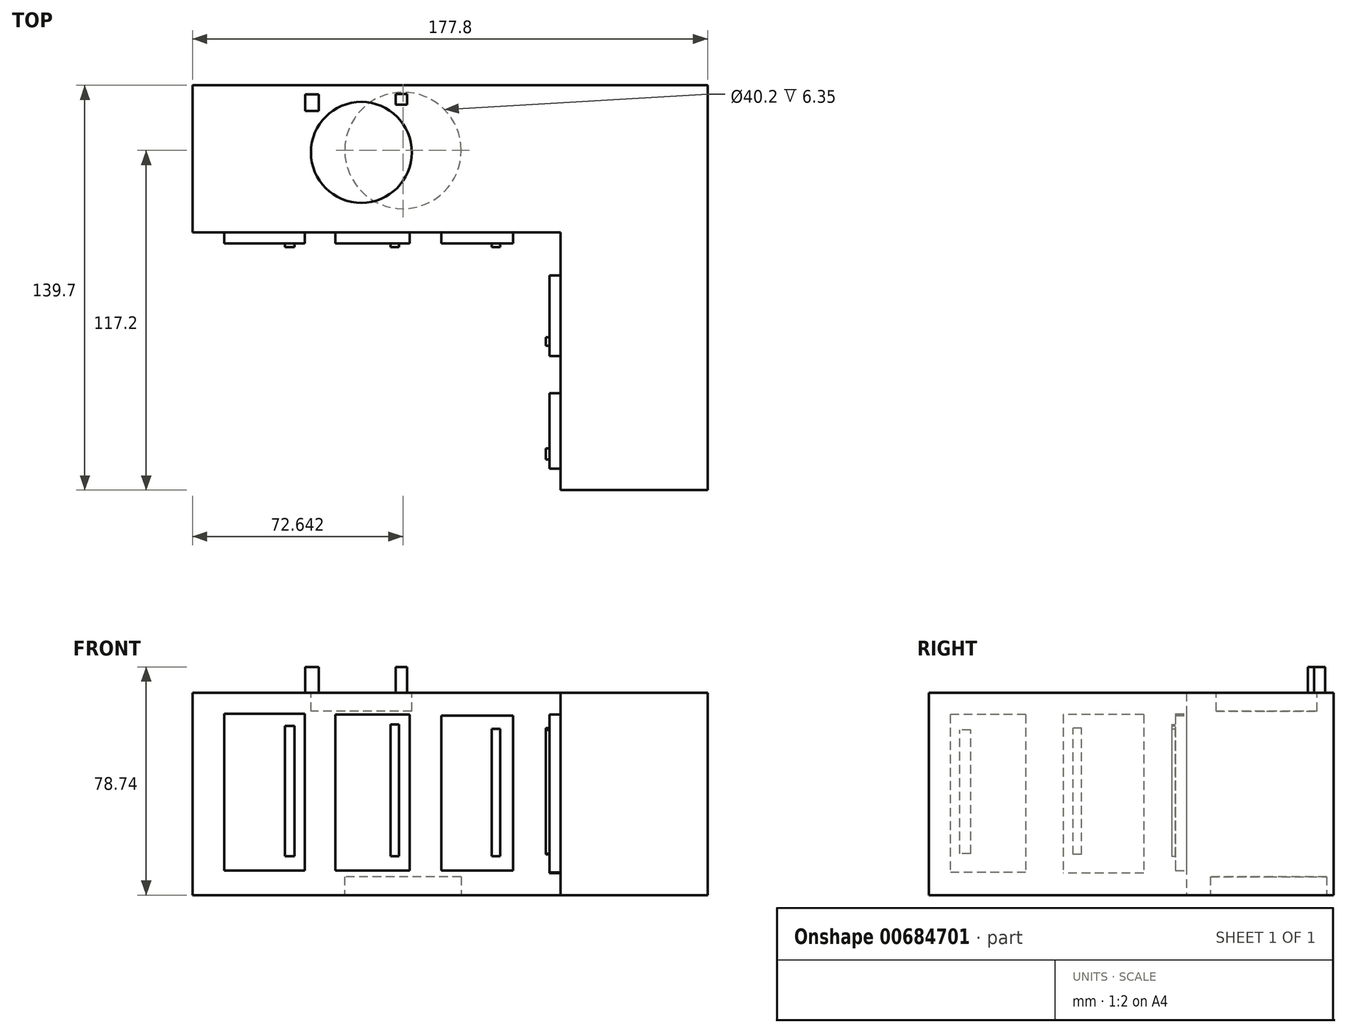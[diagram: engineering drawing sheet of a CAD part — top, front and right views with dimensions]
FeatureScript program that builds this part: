
annotation { "Feature Type Name" : "Feature", "Feature Type Description" : "" }
export const myFeature = defineFeature(function(context is Context, id is Id, definition is map)
    precondition{}
    {
        {
            var Q0;
            Q0=qCreatedBy(makeId("Top.planeOp"),FACE);
            var sketch = newSketch(context, id + "F0", { "sketchPlane" : qUnion([Q0])});
            skLineSegment(sketch, "E0.bottom", {"start": v(-90.51, 80.44) * mm, "end": v(87.29, 80.44) * mm});
            skLineSegment(sketch, "E0.top", {"start": v(-90.51, 29.64) * mm, "end": v(87.29, 29.64) * mm});
            skLineSegment(sketch, "E0.left", {"start": v(-90.51, 80.44) * mm, "end": v(-90.51, 29.64) * mm});
            skLineSegment(sketch, "E0.right", {"start": v(87.29, 80.44) * mm, "end": v(87.29, 29.64) * mm});
            skLineSegment(sketch, "E1.bottom", {"start": v(87.29, 29.64) * mm, "end": v(36.49, 29.64) * mm});
            skLineSegment(sketch, "E1.top", {"start": v(87.29, -59.26) * mm, "end": v(36.49, -59.26) * mm});
            skLineSegment(sketch, "E1.left", {"start": v(87.29, 29.64) * mm, "end": v(87.29, -59.26) * mm});
            skLineSegment(sketch, "E1.right", {"start": v(36.49, 29.64) * mm, "end": v(36.49, -59.26) * mm});
            skSolve(sketch);
        }
        {
            var Q0;
            Q0=qSketchRegion(id+"F0",true);
            extrude(context, id + "F1", {"entities" : qUnion([Q0]), "depth" : 69.85 * mm, "offsetDistance" : 25.4 * mm});
        }
        {
            var Q0;
            Q0=qCreatedBy(makeId("Top.planeOp"),FACE);
            var sketch = newSketch(context, id + "F2", { "sketchPlane" : qUnion([Q0])});
            skCircle(sketch, "E2", {"center": v(-17.87, 57.94) * mm, "radius": 20.1 * mm});
            skSolve(sketch);
        }
        {
            var Q0;
            Q0=qSketchRegion(id+"F2",true);
            extrude(context, id + "F3", {"entities" : qUnion([Q0]), "operationType" : NewBodyOperationType.REMOVE, "oppositeDirection" : true, "depth" : -6.35 * mm, "offsetDistance" : 25.4 * mm});
        }
        {
            var Q0;
            Q0=makeQuery(id+"F1.opExtrude","CAP_FACE",FACE,{"disambiguationData":[OSD([sQuery(id+"F0.wireOp",EDGE,"E0.bottom"),sQuery(id+"F0.wireOp",EDGE,"E0.top"),sQuery(id+"F0.wireOp",EDGE,"E0.left"),sQuery(id+"F0.wireOp",EDGE,"E0.right"),sQuery(id+"F0.wireOp",EDGE,"E1.top"),sQuery(id+"F0.wireOp",EDGE,"E1.left"),sQuery(id+"F0.wireOp",EDGE,"E1.right")])],"isStart":false});
            var sketch = newSketch(context, id + "F4", { "sketchPlane" : qUnion([Q0])});
            skCircle(sketch, "E3", {"center": v(-32.23, 57.3) * mm, "radius": 17.41 * mm});
            skSolve(sketch);
        }
        {
            var Q0;
            Q0=qSketchRegion(id+"F4",true);
            extrude(context, id + "F5", {"entities" : qUnion([Q0]), "operationType" : NewBodyOperationType.REMOVE, "oppositeDirection" : true, "depth" : 6.35 * mm, "offsetDistance" : 25.4 * mm});
        }
        {
            var Q0;
            Q0=makeQuery(id+"F1.opExtrude","CAP_FACE",FACE,{"disambiguationData":[OSD([sQuery(id+"F0.wireOp",EDGE,"E0.bottom"),sQuery(id+"F0.wireOp",EDGE,"E0.top"),sQuery(id+"F0.wireOp",EDGE,"E0.left"),sQuery(id+"F0.wireOp",EDGE,"E0.right"),sQuery(id+"F0.wireOp",EDGE,"E1.top"),sQuery(id+"F0.wireOp",EDGE,"E1.left"),sQuery(id+"F0.wireOp",EDGE,"E1.right")])],"isStart":false});
            var sketch = newSketch(context, id + "F6", { "sketchPlane" : qUnion([Q0])});
            skLineSegment(sketch, "E4.bottom", {"start": v(-51.56, 77.25) * mm, "end": v(-46.96, 77.25) * mm});
            skLineSegment(sketch, "E4.top", {"start": v(-51.56, 71.58) * mm, "end": v(-46.96, 71.58) * mm});
            skLineSegment(sketch, "E4.left", {"start": v(-51.56, 77.25) * mm, "end": v(-51.56, 71.58) * mm});
            skLineSegment(sketch, "E4.right", {"start": v(-46.96, 77.25) * mm, "end": v(-46.96, 71.58) * mm});
            skLineSegment(sketch, "E5.bottom", {"start": v(-20.42, 77.46) * mm, "end": v(-16.41, 77.46) * mm});
            skLineSegment(sketch, "E5.top", {"start": v(-20.42, 73.7) * mm, "end": v(-16.41, 73.7) * mm});
            skLineSegment(sketch, "E5.left", {"start": v(-20.42, 77.46) * mm, "end": v(-20.42, 73.7) * mm});
            skLineSegment(sketch, "E5.right", {"start": v(-16.41, 77.46) * mm, "end": v(-16.41, 73.7) * mm});
            skSolve(sketch);
        }
        {
            var Q0;
            Q0=qSketchRegion(id+"F6",true);
            extrude(context, id + "F7", {"entities" : qUnion([Q0]), "operationType" : NewBodyOperationType.ADD, "depth" : 8.9 * mm, "offsetDistance" : 25.4 * mm});
        }
        {
            var Q0;
            Q0=makeQuery(id+"F1.opExtrude","SWEPT_FACE",FACE,{"disambiguationData":[OSD([sQuery(id+"F0.wireOp",EDGE,"E0.top")])]});
            var sketch = newSketch(context, id + "F8", { "sketchPlane" : qUnion([Q0])});
            skLineSegment(sketch, "E6.bottom", {"start": v(-79.6, 62.57) * mm, "end": v(-51.8, 62.57) * mm});
            skLineSegment(sketch, "E6.top", {"start": v(-79.6, 8.44) * mm, "end": v(-51.8, 8.44) * mm});
            skLineSegment(sketch, "E6.left", {"start": v(-79.6, 62.57) * mm, "end": v(-79.6, 8.44) * mm});
            skLineSegment(sketch, "E6.right", {"start": v(-51.8, 62.57) * mm, "end": v(-51.8, 8.44) * mm});
            skLineSegment(sketch, "E7.bottom", {"start": v(-41.26, 62.28) * mm, "end": v(-15.51, 62.28) * mm});
            skLineSegment(sketch, "E7.top", {"start": v(-41.26, 8.44) * mm, "end": v(-15.51, 8.44) * mm});
            skLineSegment(sketch, "E7.left", {"start": v(-41.26, 62.28) * mm, "end": v(-41.26, 8.44) * mm});
            skLineSegment(sketch, "E7.right", {"start": v(-15.51, 62.28) * mm, "end": v(-15.51, 8.44) * mm});
            skLineSegment(sketch, "E8.bottom", {"start": v(-4.69, 61.99) * mm, "end": v(20.18, 61.99) * mm});
            skLineSegment(sketch, "E8.top", {"start": v(-4.69, 8.44) * mm, "end": v(20.18, 8.44) * mm});
            skLineSegment(sketch, "E8.left", {"start": v(-4.69, 61.99) * mm, "end": v(-4.69, 8.44) * mm});
            skLineSegment(sketch, "E8.right", {"start": v(20.18, 61.99) * mm, "end": v(20.18, 8.44) * mm});
            skSolve(sketch);
        }
        {
            var Q0;
            Q0=qSketchRegion(id+"F8",true);
            extrude(context, id + "F9", {"entities" : qUnion([Q0]), "operationType" : NewBodyOperationType.ADD, "depth" : 3.8 * mm, "offsetDistance" : 25.4 * mm});
        }
        {
            var Q0;
            Q0=makeQuery(id+"F1.opExtrude","SWEPT_FACE",FACE,{"disambiguationData":[OSD([sQuery(id+"F0.wireOp",EDGE,"E1.right")])]});
            var sketch = newSketch(context, id + "F10", { "sketchPlane" : qUnion([Q0])});
            skLineSegment(sketch, "E9.bottom", {"start": v(-14.85, 62.28) * mm, "end": v(12.95, 62.28) * mm});
            skLineSegment(sketch, "E9.top", {"start": v(-14.85, 7.56) * mm, "end": v(12.95, 7.56) * mm});
            skLineSegment(sketch, "E9.left", {"start": v(-14.85, 62.28) * mm, "end": v(-14.85, 7.56) * mm});
            skLineSegment(sketch, "E9.right", {"start": v(12.95, 62.28) * mm, "end": v(12.95, 7.56) * mm});
            skLineSegment(sketch, "E10.bottom", {"start": v(25.82, 62.28) * mm, "end": v(51.86, 62.28) * mm});
            skLineSegment(sketch, "E10.top", {"start": v(25.82, 7.85) * mm, "end": v(51.86, 7.85) * mm});
            skLineSegment(sketch, "E10.left", {"start": v(25.82, 62.28) * mm, "end": v(25.82, 7.85) * mm});
            skLineSegment(sketch, "E10.right", {"start": v(51.86, 62.28) * mm, "end": v(51.86, 7.85) * mm});
            skSolve(sketch);
        }
        {
            var Q0;
            Q0=qSketchRegion(id+"F10",true);
            extrude(context, id + "F11", {"entities" : qUnion([Q0]), "operationType" : NewBodyOperationType.ADD, "depth" : 3.8 * mm, "offsetDistance" : 25.4 * mm});
        }
        {
            var Q0;
            Q0=makeQuery(id+"F1.opExtrude","SWEPT_FACE",FACE,{"disambiguationData":[OSD([sQuery(id+"F0.wireOp",EDGE,"E0.top")])]});
            var sketch = newSketch(context, id + "F12", { "sketchPlane" : qUnion([Q0])});
            skLineSegment(sketch, "E11.bottom", {"start": v(-58.65, 58.4) * mm, "end": v(-55.35, 58.4) * mm});
            skLineSegment(sketch, "E11.top", {"start": v(-58.65, 13.35) * mm, "end": v(-55.35, 13.35) * mm});
            skLineSegment(sketch, "E11.left", {"start": v(-58.65, 58.4) * mm, "end": v(-58.65, 13.35) * mm});
            skLineSegment(sketch, "E11.right", {"start": v(-55.35, 58.4) * mm, "end": v(-55.35, 13.35) * mm});
            skLineSegment(sketch, "E12.bottom", {"start": v(-19.29, 58.92) * mm, "end": v(-22.15, 58.92) * mm});
            skLineSegment(sketch, "E12.top", {"start": v(-19.29, 13.35) * mm, "end": v(-22.15, 13.35) * mm});
            skLineSegment(sketch, "E12.left", {"start": v(-19.29, 58.92) * mm, "end": v(-19.29, 13.35) * mm});
            skLineSegment(sketch, "E12.right", {"start": v(-22.15, 58.92) * mm, "end": v(-22.15, 13.35) * mm});
            skLineSegment(sketch, "E13.bottom", {"start": v(15.65, 57.4) * mm, "end": v(12.77, 57.4) * mm});
            skLineSegment(sketch, "E13.top", {"start": v(15.65, 13.35) * mm, "end": v(12.77, 13.35) * mm});
            skLineSegment(sketch, "E13.left", {"start": v(15.65, 57.4) * mm, "end": v(15.65, 13.35) * mm});
            skLineSegment(sketch, "E13.right", {"start": v(12.77, 57.4) * mm, "end": v(12.77, 13.35) * mm});
            skSolve(sketch);
        }
        {
            var Q0;
            Q0=qSketchRegion(id+"F12",true);
            extrude(context, id + "F13", {"entities" : qUnion([Q0]), "operationType" : NewBodyOperationType.ADD, "depth" : 5.08 * mm, "offsetDistance" : 25.4 * mm});
        }
        {
            var Q0;
            Q0=makeQuery(id+"F1.opExtrude","SWEPT_FACE",FACE,{"disambiguationData":[OSD([sQuery(id+"F0.wireOp",EDGE,"E1.right")])]});
            var sketch = newSketch(context, id + "F14", { "sketchPlane" : qUnion([Q0])});
            skLineSegment(sketch, "E14.bottom", {"start": v(9.44, 57.6) * mm, "end": v(6.51, 57.6) * mm});
            skLineSegment(sketch, "E14.top", {"start": v(9.44, 14) * mm, "end": v(6.51, 14) * mm});
            skLineSegment(sketch, "E14.left", {"start": v(9.44, 57.6) * mm, "end": v(9.44, 14) * mm});
            skLineSegment(sketch, "E14.right", {"start": v(6.51, 57.6) * mm, "end": v(6.51, 14) * mm});
            skLineSegment(sketch, "E15.bottom", {"start": v(48.65, 57.01) * mm, "end": v(44.84, 57.01) * mm});
            skLineSegment(sketch, "E15.top", {"start": v(48.65, 14.3) * mm, "end": v(44.84, 14.3) * mm});
            skLineSegment(sketch, "E15.left", {"start": v(48.65, 57.01) * mm, "end": v(48.65, 14.3) * mm});
            skLineSegment(sketch, "E15.right", {"start": v(44.84, 57.01) * mm, "end": v(44.84, 14.3) * mm});
            skSolve(sketch);
        }
        {
            var Q0;
            Q0=qSketchRegion(id+"F14",true);
            extrude(context, id + "F15", {"entities" : qUnion([Q0]), "operationType" : NewBodyOperationType.ADD, "depth" : 5.08 * mm, "offsetDistance" : 25.4 * mm});
        }
    });
